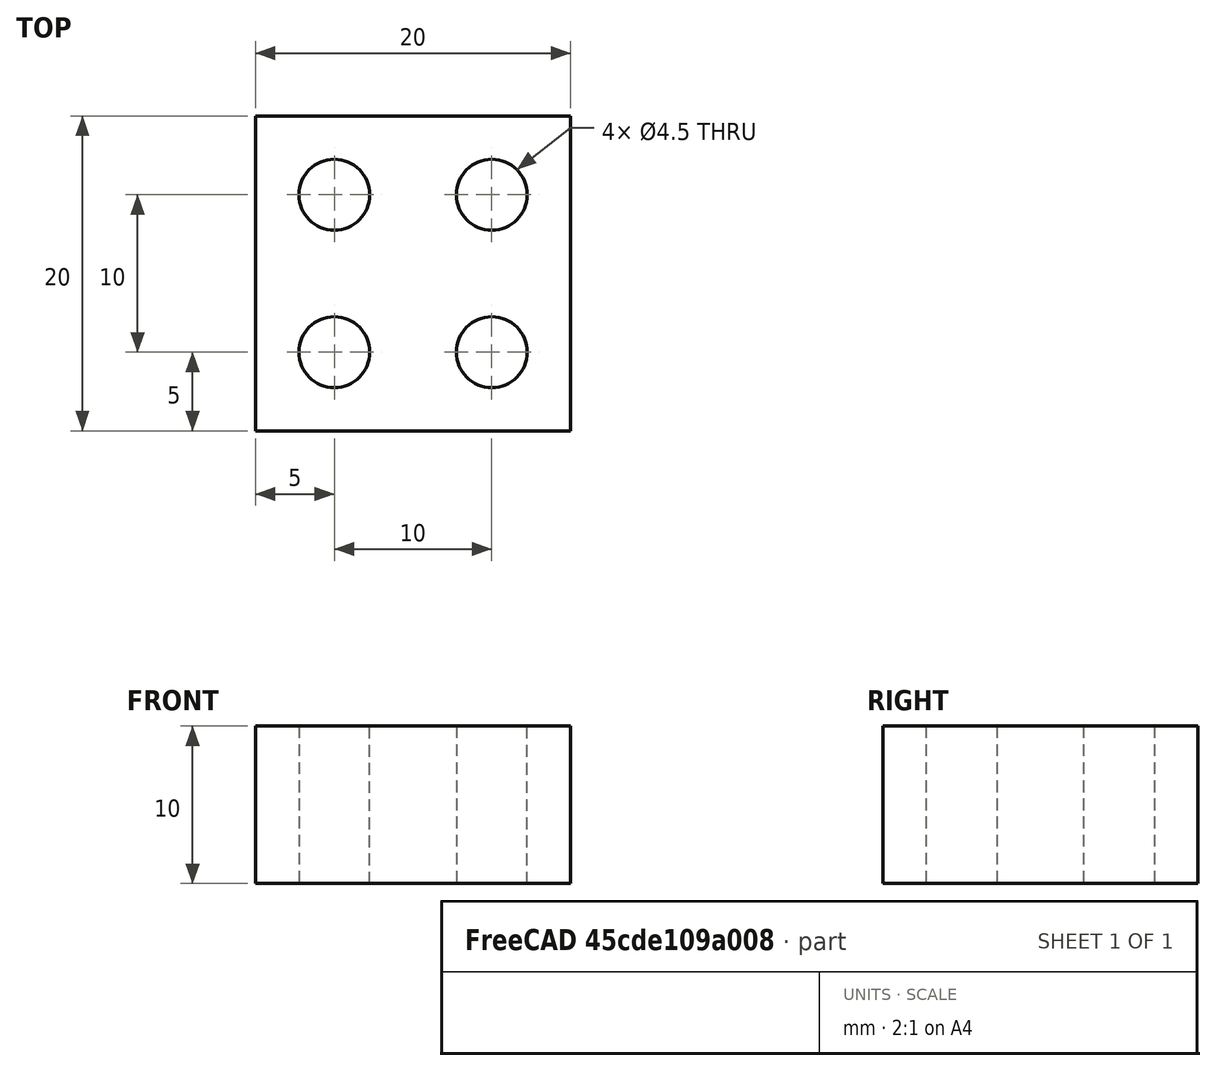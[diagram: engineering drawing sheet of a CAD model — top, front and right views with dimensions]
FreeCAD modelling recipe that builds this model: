
FCSTD DOCUMENT  (FreeCAD 0.21R33771 (Git))
Label: parametric_square_drill_jig
License: All rights reserved
LicenseURL: http://en.wikipedia.org/wiki/All_rights_reserved
objects: Spreadsheet::Sheet×1, Sketcher::SketchObject×1, PartDesign::Pad×1, PartDesign::Body×1
note: 4 computed .brp shape members not serialized (recipe doc carries the construction recipe); baked Part::Feature solids carry a one-line shape summary decoded from their .brp

FEATURE [Spreadsheet::Sheet] Spreadsheet  label="settings"
  cells = A1='Plate; C1='Holes; A2='X size; B2(plate_size_x)=20; C2='X spacing; D2(hole_spacing_x)=10; A3='Y size; B3(plate_size_y)=20; C3='Y spacing; D3(hole_spacing_y)=10; A4='Thickness; B4(plate_thickness)=10; C4='Diameter; D4(hole_diameter)=4.5
FEATURE [Sketcher::SketchObject] Sketch
  FullyConstrained = true
  MapMode = 5
  Support = -> [XY_Plane]
  expr: Constraints[10] = <<settings>>.plate_size_y
  expr: Constraints[20] = <<settings>>.hole_spacing_x
  expr: Constraints[21] = <<settings>>.hole_spacing_y
  expr: Constraints[29] = <<settings>>.hole_diameter
  expr: Constraints[8] = <<settings>>.plate_size_x
  sketch-geometry (12):
    g0: LineSegment StartX=-10 StartY=10 StartZ=0 EndX=10 EndY=10 EndZ=0
    g1: LineSegment StartX=10 StartY=10 StartZ=0 EndX=10 EndY=-10 EndZ=0
    g2: LineSegment StartX=10 StartY=-10 StartZ=0 EndX=-10 EndY=-10 EndZ=0
    g3: LineSegment StartX=-10 StartY=-10 StartZ=0 EndX=-10 EndY=10 EndZ=0
    g4: LineSegment StartX=-5 StartY=5 StartZ=0 EndX=5 EndY=5 EndZ=0
    g5: LineSegment StartX=5 StartY=5 StartZ=0 EndX=5 EndY=-5 EndZ=0
    g6: LineSegment StartX=5 StartY=-5 StartZ=0 EndX=-5 EndY=-5 EndZ=0
    g7: LineSegment StartX=-5 StartY=-5 StartZ=0 EndX=-5 EndY=5 EndZ=0
    g8: Circle CenterX=-5 CenterY=5 CenterZ=0 NormalX=0 NormalY=0 NormalZ=1 AngleXU=0 Radius=2.25
    g9: Circle CenterX=5 CenterY=5 CenterZ=0 NormalX=0 NormalY=0 NormalZ=1 AngleXU=0 Radius=2.25
    g10: Circle CenterX=5 CenterY=-5 CenterZ=0 NormalX=0 NormalY=0 NormalZ=1 AngleXU=0 Radius=2.25
    g11: Circle CenterX=-5 CenterY=-5 CenterZ=0 NormalX=0 NormalY=0 NormalZ=1 AngleXU=0 Radius=2.25
  constraints (30):
    c: Coincident(g0,g1)
    c: Coincident(g1,g2)
    c: Coincident(g2,g3)
    c: Coincident(g3,g0)
    c: Horizontal(g0)
    c: Horizontal(g2)
    c: Vertical(g1)
    c: Vertical(g3)
    c: DistanceX(g0,g0) = 20
    c: Symmetric(g0,g2,g-1)
    c: DistanceY(g1,g1) = 20
    c: Coincident(g4,g5)
    c: Coincident(g5,g6)
    c: Coincident(g6,g7)
    c: Coincident(g7,g4)
    c: Horizontal(g4)
    c: Horizontal(g6)
    c: Vertical(g5)
    c: Vertical(g7)
    c: Symmetric(g4,g6,g-1)
    c: DistanceX(g4,g4) = 10
    c: DistanceY(g5,g5) = 10
    c: Coincident(g8,g4)
    c: Coincident(g9,g4)
    c: Coincident(g10,g5)
    c: Coincident(g11,g6)
    c: Equal(g8,g11)
    c: Equal(g8,g9)
    c: Equal(g8,g10)
    c: Diameter(g8) = 4.5
FEATURE [PartDesign::Pad] Pad  label="jig_pad"
  Direction = (0,0,1)
  Length = 10
  Length2 = 10
  Profile = -> Sketch
  ReferenceAxis = -> Sketch [N_Axis]
  Type = 0
  expr: Length = <<settings>>.plate_thickness
FEATURE [PartDesign::Body] Body
  Group = -> [Sketch,Pad]
  Origin = -> Origin
  Tip = -> Pad
